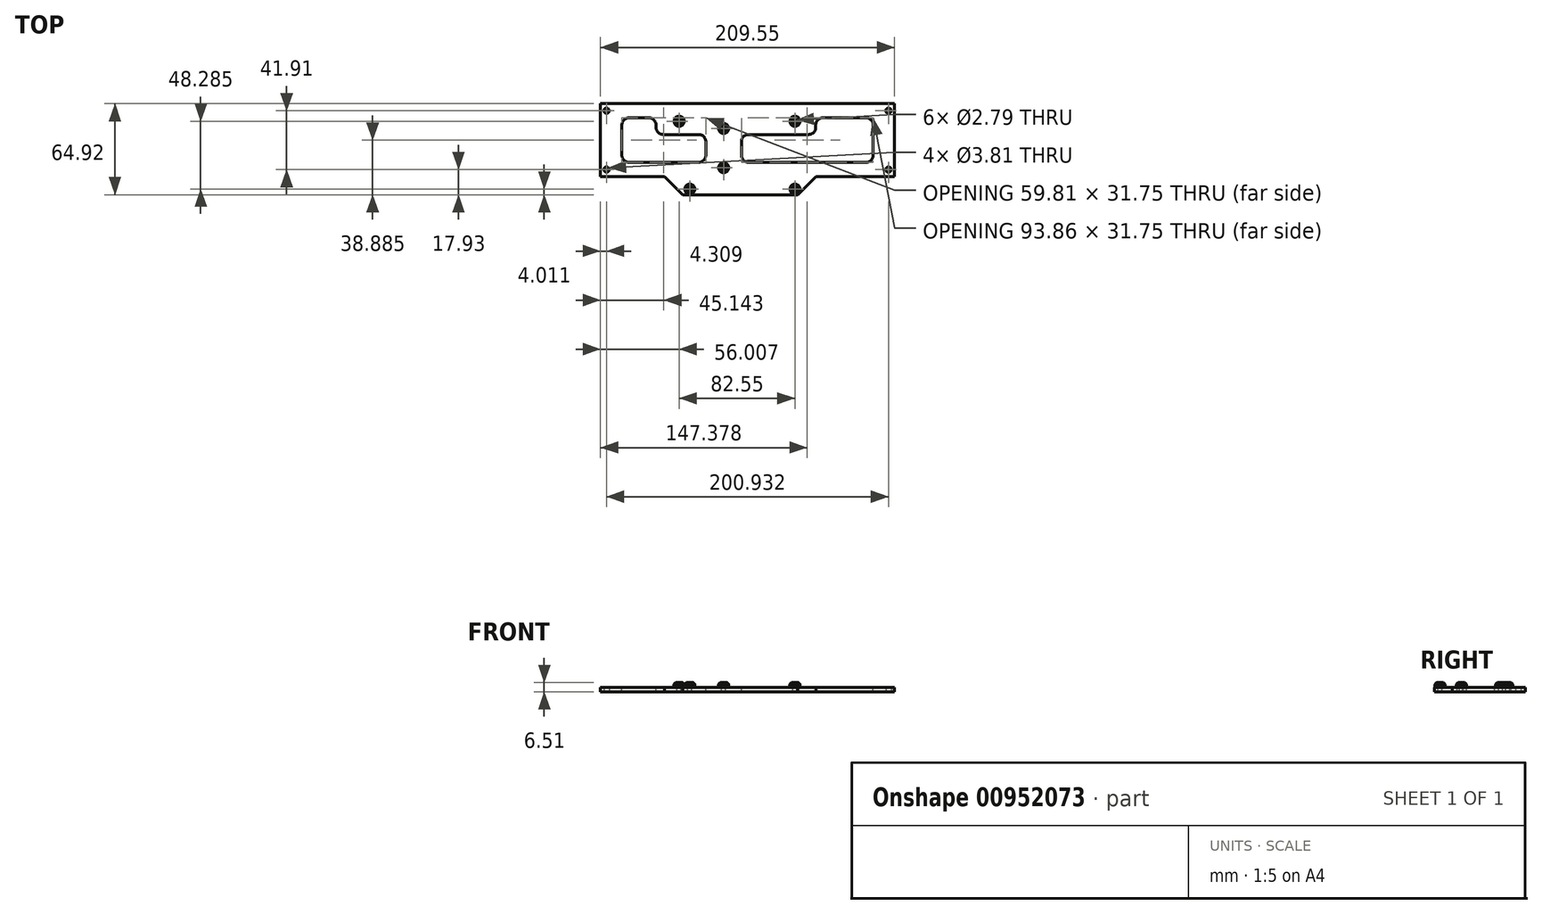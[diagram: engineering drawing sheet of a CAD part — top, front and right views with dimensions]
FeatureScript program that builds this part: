
annotation { "Feature Type Name" : "Feature", "Feature Type Description" : "" }
export const myFeature = defineFeature(function(context is Context, id is Id, definition is map)
    precondition{}
    {
        {
            var Q0;
            Q0=qCreatedBy(makeId("Top.planeOp"),FACE);
            var sketch = newSketch(context, id + "F0", { "sketchPlane" : qUnion([Q0])});
            skLineSegment(sketch, "E0.bottom", {"start": v(0, 0) * mm, "end": v(-209.55, 0) * mm});
            skLineSegment(sketch, "E0.top", {"start": v(0, -52.07) * mm, "end": v(-209.55, -52.07) * mm});
            skLineSegment(sketch, "E0.left", {"start": v(0, 0) * mm, "end": v(0, -52.07) * mm});
            skLineSegment(sketch, "E0.right", {"start": v(-209.55, 0) * mm, "end": v(-209.55, -52.07) * mm});
            skCircle(sketch, "E1", {"center": v(-205.24, -5.08) * mm, "radius": 1.9 * mm});
            skCircle(sketch, "E2", {"center": v(-4.3, -5.08) * mm, "radius": 1.9 * mm});
            skCircle(sketch, "E3", {"center": v(-205.24, -47) * mm, "radius": 1.9 * mm});
            skCircle(sketch, "E4", {"center": v(-4.3, -47) * mm, "radius": 1.9 * mm});
            skLineSegment(sketch, "E5", {"start": v(-4.3, -5.08) * mm, "end": v(0, -5.08) * mm, "construction": true});
            skLineSegment(sketch, "E6", {"start": v(-205.24, -5.08) * mm, "end": v(-209.55, -5.08) * mm, "construction": true});
            skLineSegment(sketch, "E7", {"start": v(-205.24, -5.08) * mm, "end": v(-205.24, 0) * mm, "construction": true});
            skLineSegment(sketch, "E8", {"start": v(-205.24, -47) * mm, "end": v(-205.24, -52.07) * mm, "construction": true});
            skSolve(sketch);
        }
        {
            var Q0;
            Q0 = qSketchRegion(id + "F0", true);
            extrude(context, id + "F1", {"entities" : qUnion([Q0]), "depth" : 3 * mm, "offsetDistance" : 25.4 * mm});
        }
        {
            var Q0;
            Q0=makeQuery(id+"F1.opExtrude","CAP_FACE",FACE,{"disambiguationData":[OSD([sQuery(id+"F0.wireOp",EDGE,"E0.bottom"),sQuery(id+"F0.wireOp",EDGE,"E0.top"),sQuery(id+"F0.wireOp",EDGE,"E0.left"),sQuery(id+"F0.wireOp",EDGE,"E0.right"),sQuery(id+"F0.wireOp",EDGE,"E1"),sQuery(id+"F0.wireOp",EDGE,"E2"),sQuery(id+"F0.wireOp",EDGE,"E3"),sQuery(id+"F0.wireOp",EDGE,"E4")])],"isStart":false});
            var sketch = newSketch(context, id + "F2", { "sketchPlane" : qUnion([Q0])});
            skLineSegment(sketch, "E9", {"start": v(-163.86, -52.07) * mm, "end": v(-151, -64.92) * mm});
            skLineSegment(sketch, "E10", {"start": v(-151, -64.92) * mm, "end": v(-68.9, -64.92) * mm});
            skLineSegment(sketch, "E11", {"start": v(-68.9, -64.92) * mm, "end": v(-56.03, -52.07) * mm});
            skLineSegment(sketch, "E12", {"start": v(-163.86, -52.07) * mm, "end": v(-56.03, -52.07) * mm});
            skSolve(sketch);
        }
        {
            var Q0;
            Q0 = qSketchRegion(id + "F2", true);
            var Q1;
            Q1=makeQuery(id+"F1.opExtrude","CAP_FACE",FACE,{"disambiguationData":[OSD([sQuery(id+"F0.wireOp",EDGE,"E0.bottom"),sQuery(id+"F0.wireOp",EDGE,"E0.top"),sQuery(id+"F0.wireOp",EDGE,"E0.left"),sQuery(id+"F0.wireOp",EDGE,"E0.right"),sQuery(id+"F0.wireOp",EDGE,"E1"),sQuery(id+"F0.wireOp",EDGE,"E2"),sQuery(id+"F0.wireOp",EDGE,"E3"),sQuery(id+"F0.wireOp",EDGE,"E4")])],"isStart":true});
            extrude(context, id + "F3", {"entities" : qUnion([Q0]), "operationType" : NewBodyOperationType.ADD, "endBound" : BoundingType.UP_TO_SURFACE, "oppositeDirection" : true, "depth" : 25.4 * mm, "endBoundEntityFace" : qUnion([Q1]), "offsetDistance" : 25.4 * mm});
        }
        {
            var Q0;
            Q0=makeQuery(id+"F3.boolean.opBoolean","MERGE",FACE,{"derivedFrom":[makeQuery(id+"F1.opExtrude","CAP_FACE",FACE,{"disambiguationData":[OSD([sQuery(id+"F0.wireOp",EDGE,"E0.bottom"),sQuery(id+"F0.wireOp",EDGE,"E0.top"),sQuery(id+"F0.wireOp",EDGE,"E0.left"),sQuery(id+"F0.wireOp",EDGE,"E0.right"),sQuery(id+"F0.wireOp",EDGE,"E1"),sQuery(id+"F0.wireOp",EDGE,"E2"),sQuery(id+"F0.wireOp",EDGE,"E3"),sQuery(id+"F0.wireOp",EDGE,"E4")])],"isStart":false}),makeQuery(id+"F3.opExtrude","CAP_FACE",FACE,{"disambiguationData":[OSD([sQuery(id+"F2.wireOp",EDGE,"E9"),sQuery(id+"F2.wireOp",EDGE,"E10"),sQuery(id+"F2.wireOp",EDGE,"E11"),sQuery(id+"F2.wireOp",EDGE,"E12")])],"isStart":true})]});
            var sketch = newSketch(context, id + "F4", { "sketchPlane" : qUnion([Q0])});
            skCircle(sketch, "E13", {"center": v(-71, -12.62) * mm, "radius": 1.4 * mm});
            skCircle(sketch, "E14", {"center": v(-71, -60.9) * mm, "radius": 1.4 * mm});
            skCircle(sketch, "E15", {"center": v(-153.54, -12.62) * mm, "radius": 1.4 * mm});
            skCircle(sketch, "E16", {"center": v(-145.92, -60.9) * mm, "radius": 1.4 * mm});
            skCircle(sketch, "E17", {"center": v(-121.8, -45.66) * mm, "radius": 1.4 * mm});
            skLineSegment(sketch, "E18", {"start": v(-71, -60.9) * mm, "end": v(-104.02, -27.88) * mm});
            skLineSegment(sketch, "E19", {"start": v(-104.02, -27.88) * mm, "end": v(-121.8, -45.66) * mm});
            skCircle(sketch, "E20", {"center": v(-121.8, -17.72) * mm, "radius": 1.4 * mm});
            skSolve(sketch);
        }
        {
            var Q0;
            Q0 = qSketchRegion(id + "F4", true);
            extrude(context, id + "F5", {"entities" : qUnion([Q0]), "operationType" : NewBodyOperationType.REMOVE, "oppositeDirection" : true, "depth" : 25.4 * mm, "offsetDistance" : 25.4 * mm});
        }
        {
            var Q0;
            Q0=makeQuery(id+"F3.boolean.opBoolean","MERGE",FACE,{"derivedFrom":[makeQuery(id+"F1.opExtrude","CAP_FACE",FACE,{"disambiguationData":[OSD([sQuery(id+"F0.wireOp",EDGE,"E0.bottom"),sQuery(id+"F0.wireOp",EDGE,"E0.top"),sQuery(id+"F0.wireOp",EDGE,"E0.left"),sQuery(id+"F0.wireOp",EDGE,"E0.right"),sQuery(id+"F0.wireOp",EDGE,"E1"),sQuery(id+"F0.wireOp",EDGE,"E2"),sQuery(id+"F0.wireOp",EDGE,"E3"),sQuery(id+"F0.wireOp",EDGE,"E4")])],"isStart":false}),makeQuery(id+"F3.opExtrude","CAP_FACE",FACE,{"disambiguationData":[OSD([sQuery(id+"F2.wireOp",EDGE,"E9"),sQuery(id+"F2.wireOp",EDGE,"E10"),sQuery(id+"F2.wireOp",EDGE,"E11"),sQuery(id+"F2.wireOp",EDGE,"E12")])],"isStart":true})]});
            var sketch = newSketch(context, id + "F6", { "sketchPlane" : qUnion([Q0])});
            skCircle(sketch, "E21.0", {"center": v(-153.54, -12.62) * mm, "radius": 1.4 * mm});
            skCircle(sketch, "E22.0", {"center": v(-121.8, -17.72) * mm, "radius": 1.4 * mm});
            skCircle(sketch, "E23.0", {"center": v(-121.8, -45.66) * mm, "radius": 1.4 * mm});
            skCircle(sketch, "E24.0", {"center": v(-145.92, -60.9) * mm, "radius": 1.4 * mm});
            skCircle(sketch, "E25.0", {"center": v(-71, -60.9) * mm, "radius": 1.4 * mm});
            skCircle(sketch, "E26.0", {"center": v(-71, -12.62) * mm, "radius": 1.4 * mm});
            skCircle(sketch, "E27", {"center": v(-153.54, -12.62) * mm, "radius": 3.62 * mm});
            skCircle(sketch, "E28", {"center": v(-145.92, -60.9) * mm, "radius": 3.62 * mm});
            skCircle(sketch, "E29", {"center": v(-121.8, -45.66) * mm, "radius": 3.62 * mm});
            skCircle(sketch, "E30", {"center": v(-121.8, -17.72) * mm, "radius": 3.62 * mm});
            skCircle(sketch, "E31", {"center": v(-71, -12.62) * mm, "radius": 3.62 * mm});
            skCircle(sketch, "E32", {"center": v(-71, -60.9) * mm, "radius": 3.62 * mm});
            skSolve(sketch);
        }
        {
            var Q0;
            Q0 = qSketchRegion(id + "F6", true);
            extrude(context, id + "F7", {"entities" : qUnion([Q0]), "operationType" : NewBodyOperationType.ADD, "depth" : 3.5 * mm, "offsetDistance" : 25.4 * mm});
        }
        {
            var Q0;
            Q0=makeQuery(id+"F7.opExtrude","CAP_EDGE",EDGE,{"disambiguationData":[OSD([sQuery(id+"F6.wireOp",EDGE,"E27")])],"isStart":false});
            var Q1;
            Q1=makeQuery(id+"F7.opExtrude","CAP_EDGE",EDGE,{"disambiguationData":[OSD([sQuery(id+"F6.wireOp",EDGE,"E30")])],"isStart":false});
            var Q2;
            Q2=makeQuery(id+"F7.opExtrude","CAP_EDGE",EDGE,{"disambiguationData":[OSD([sQuery(id+"F6.wireOp",EDGE,"E29")])],"isStart":false});
            var Q3;
            Q3=makeQuery(id+"F7.opExtrude","CAP_EDGE",EDGE,{"disambiguationData":[OSD([sQuery(id+"F6.wireOp",EDGE,"E28")])],"isStart":false});
            var Q4;
            Q4=makeQuery(id+"F7.opExtrude","CAP_EDGE",EDGE,{"disambiguationData":[OSD([sQuery(id+"F6.wireOp",EDGE,"E32")])],"isStart":false});
            var Q5;
            Q5=makeQuery(id+"F7.opExtrude","CAP_EDGE",EDGE,{"disambiguationData":[OSD([sQuery(id+"F6.wireOp",EDGE,"E31")])],"isStart":false});
            chamfer(context, id + "F8", {"entities" : qUnion([Q0, Q1, Q2, Q3, Q4, Q5]), "width" : 1.14 * mm, "tangentPropagation" : true});
        }
        {
            var Q0;
            Q0=makeQuery(id+"F3.boolean.opBoolean","MERGE",FACE,{"derivedFrom":[makeQuery(id+"F1.opExtrude","CAP_FACE",FACE,{"disambiguationData":[OSD([sQuery(id+"F0.wireOp",EDGE,"E0.bottom"),sQuery(id+"F0.wireOp",EDGE,"E0.top"),sQuery(id+"F0.wireOp",EDGE,"E0.left"),sQuery(id+"F0.wireOp",EDGE,"E0.right"),sQuery(id+"F0.wireOp",EDGE,"E1"),sQuery(id+"F0.wireOp",EDGE,"E2"),sQuery(id+"F0.wireOp",EDGE,"E3"),sQuery(id+"F0.wireOp",EDGE,"E4")])],"isStart":false}),makeQuery(id+"F3.opExtrude","CAP_FACE",FACE,{"disambiguationData":[OSD([sQuery(id+"F2.wireOp",EDGE,"E9"),sQuery(id+"F2.wireOp",EDGE,"E10"),sQuery(id+"F2.wireOp",EDGE,"E11"),sQuery(id+"F2.wireOp",EDGE,"E12")])],"isStart":true})]});
            var sketch = newSketch(context, id + "F9", { "sketchPlane" : qUnion([Q0])});
            skLineSegment(sketch, "E33.bottom", {"start": v(-20.32, -10.16) * mm, "end": v(-51.1, -10.16) * mm});
            skLineSegment(sketch, "E33.top", {"start": v(-20.32, -41.9) * mm, "end": v(-56.18, -41.9) * mm});
            skLineSegment(sketch, "E33.left", {"start": v(-15.24, -15.24) * mm, "end": v(-15.24, -36.83) * mm});
            skLineSegment(sketch, "E33.right", {"start": v(-56.18, -15.24) * mm, "end": v(-56.18, -16.95) * mm});
            skLineSegment(sketch, "E34.bottom", {"start": v(-189.23, -10.16) * mm, "end": v(-175.02, -10.16) * mm});
            skLineSegment(sketch, "E34.top", {"start": v(-189.23, -41.9) * mm, "end": v(-169.94, -41.9) * mm});
            skLineSegment(sketch, "E34.left", {"start": v(-194.3, -15.24) * mm, "end": v(-194.3, -36.83) * mm});
            skLineSegment(sketch, "E34.right", {"start": v(-169.94, -15.24) * mm, "end": v(-169.94, -16.95) * mm});
            skLineSegment(sketch, "E35", {"start": v(-194.3, -10.16) * mm, "end": v(-194.3, 0) * mm, "construction": true});
            skLineSegment(sketch, "E36", {"start": v(-194.3, -41.9) * mm, "end": v(-194.3, -52.07) * mm, "construction": true});
            skLineSegment(sketch, "E37.bottom", {"start": v(-169.94, -41.9) * mm, "end": v(-139.58, -41.9) * mm});
            skLineSegment(sketch, "E37.top", {"start": v(-164.86, -22.03) * mm, "end": v(-139.58, -22.03) * mm});
            skLineSegment(sketch, "E37.right", {"start": v(-134.5, -36.83) * mm, "end": v(-134.5, -27.11) * mm});
            skLineSegment(sketch, "E38.bottom", {"start": v(-56.18, -41.9) * mm, "end": v(-104.02, -41.9) * mm});
            skLineSegment(sketch, "E38.top", {"start": v(-61.26, -22.03) * mm, "end": v(-104.02, -22.03) * mm});
            skLineSegment(sketch, "E38.right", {"start": v(-109.1, -36.83) * mm, "end": v(-109.1, -27.11) * mm});
            skLineSegment(sketch, "E39", {"start": v(-121.8, -17.72) * mm, "end": v(-121.8, -45.66) * mm, "construction": true});
            skLineSegment(sketch, "E40", {"start": v(-121.8, -33.56) * mm, "end": v(-109.1, -33.56) * mm, "construction": true});
            skLineSegment(sketch, "E41", {"start": v(-121.8, -33.56) * mm, "end": v(-134.5, -33.56) * mm, "construction": true});
            skPoint(sketch, "E42.visualSharp", {"position": v(-56.18, -10.16) * mm});
            skArc(sketch, "E42.filletArc", {"start": v(-51.1, -10.16) * mm, "mid": v(-54.69, -11.65) * mm, "end": v(-56.18, -15.24) * mm});
            skPoint(sketch, "E43.visualSharp", {"position": v(-56.18, -22.03) * mm});
            skArc(sketch, "E43.filletArc", {"start": v(-61.26, -22.03) * mm, "mid": v(-57.66, -20.54) * mm, "end": v(-56.18, -16.95) * mm});
            skPoint(sketch, "E44.visualSharp", {"position": v(-109.1, -22.03) * mm});
            skArc(sketch, "E44.filletArc", {"start": v(-104.02, -22.03) * mm, "mid": v(-107.62, -23.52) * mm, "end": v(-109.1, -27.11) * mm});
            skPoint(sketch, "E45.visualSharp", {"position": v(-109.1, -41.9) * mm});
            skArc(sketch, "E45.filletArc", {"start": v(-109.1, -36.83) * mm, "mid": v(-107.62, -40.42) * mm, "end": v(-104.02, -41.9) * mm});
            skPoint(sketch, "E46.visualSharp", {"position": v(-15.24, -41.9) * mm});
            skArc(sketch, "E46.filletArc", {"start": v(-20.32, -41.9) * mm, "mid": v(-16.73, -40.42) * mm, "end": v(-15.24, -36.83) * mm});
            skPoint(sketch, "E47.visualSharp", {"position": v(-15.24, -10.16) * mm});
            skArc(sketch, "E47.filletArc", {"start": v(-15.24, -15.24) * mm, "mid": v(-16.73, -11.65) * mm, "end": v(-20.32, -10.16) * mm});
            skPoint(sketch, "E48.visualSharp", {"position": v(-134.5, -22.03) * mm});
            skArc(sketch, "E48.filletArc", {"start": v(-134.5, -27.11) * mm, "mid": v(-136, -23.52) * mm, "end": v(-139.58, -22.03) * mm});
            skPoint(sketch, "E49.visualSharp", {"position": v(-169.94, -22.03) * mm});
            skArc(sketch, "E49.filletArc", {"start": v(-169.94, -16.95) * mm, "mid": v(-168.45, -20.54) * mm, "end": v(-164.86, -22.03) * mm});
            skPoint(sketch, "E50.visualSharp", {"position": v(-169.94, -10.16) * mm});
            skArc(sketch, "E50.filletArc", {"start": v(-169.94, -15.24) * mm, "mid": v(-171.43, -11.65) * mm, "end": v(-175.02, -10.16) * mm});
            skPoint(sketch, "E51.visualSharp", {"position": v(-134.5, -41.9) * mm});
            skArc(sketch, "E51.filletArc", {"start": v(-139.58, -41.9) * mm, "mid": v(-136, -40.42) * mm, "end": v(-134.5, -36.83) * mm});
            skPoint(sketch, "E52.visualSharp", {"position": v(-194.3, -41.9) * mm});
            skArc(sketch, "E52.filletArc", {"start": v(-194.3, -36.83) * mm, "mid": v(-192.82, -40.42) * mm, "end": v(-189.23, -41.9) * mm});
            skPoint(sketch, "E53.visualSharp", {"position": v(-194.3, -10.16) * mm});
            skArc(sketch, "E53.filletArc", {"start": v(-189.23, -10.16) * mm, "mid": v(-192.82, -11.65) * mm, "end": v(-194.3, -15.24) * mm});
            skSolve(sketch);
        }
        {
            var Q0;
            Q0 = qSketchRegion(id + "F9", true);
            extrude(context, id + "F10", {"entities" : qUnion([Q0]), "operationType" : NewBodyOperationType.REMOVE, "oppositeDirection" : true, "depth" : 25.4 * mm, "offsetDistance" : 25.4 * mm});
        }
    });
